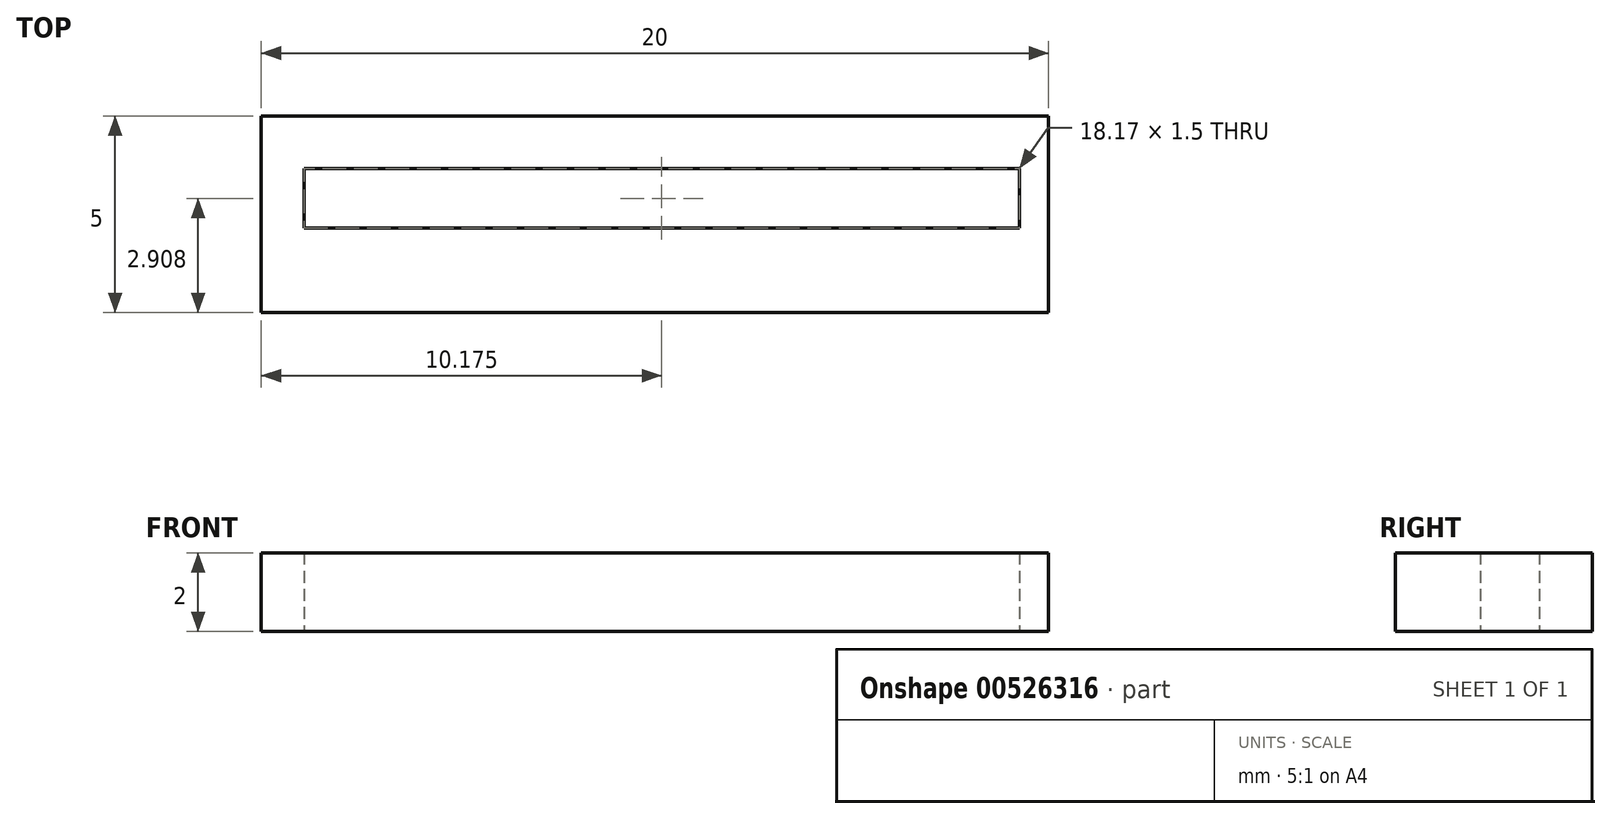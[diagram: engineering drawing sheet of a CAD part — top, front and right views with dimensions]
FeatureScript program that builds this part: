
annotation { "Feature Type Name" : "Feature", "Feature Type Description" : "" }
export const myFeature = defineFeature(function(context is Context, id is Id, definition is map)
    precondition{}
    {
        {
            var Q0;
            Q0=qCreatedBy(makeId("Top.planeOp"),FACE);
            var sketch = newSketch(context, id + "F0", { "sketchPlane" : qUnion([Q0])});
            skLineSegment(sketch, "E0.bottom", {"start": v(0, 0) * mm, "end": v(20, 0) * mm});
            skLineSegment(sketch, "E0.top", {"start": v(0, 5) * mm, "end": v(20, 5) * mm});
            skLineSegment(sketch, "E0.left", {"start": v(0, 0) * mm, "end": v(0, 5) * mm});
            skLineSegment(sketch, "E0.right", {"start": v(20, 0) * mm, "end": v(20, 5) * mm});
            skLineSegment(sketch, "E1.bottom", {"start": v(1.09, 3.66) * mm, "end": v(19.26, 3.66) * mm});
            skLineSegment(sketch, "E1.top", {"start": v(1.09, 2.16) * mm, "end": v(19.26, 2.16) * mm});
            skLineSegment(sketch, "E1.left", {"start": v(1.09, 3.66) * mm, "end": v(1.09, 2.16) * mm});
            skLineSegment(sketch, "E1.right", {"start": v(19.26, 3.66) * mm, "end": v(19.26, 2.16) * mm});
            skSolve(sketch);
        }
        {
            var Q0;
            Q0=makeQuery(id+"F0.imprint","IMPRINT",FACE,{"disambiguationData":[TD([[makeQuery(id+"F0.imprint","IMPRINT",EDGE,{"derivedFrom":sQuery(id+"F0.wireOp",EDGE,"E0.bottom")}),1.0]])]});
            extrude(context, id + "F1", {"entities" : qUnion([Q0]), "depth" : 2 * mm, "offsetDistance" : 25 * mm});
        }
    });
